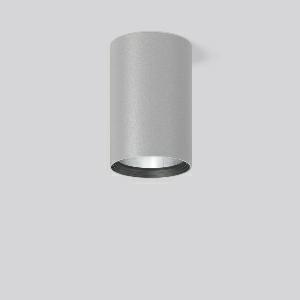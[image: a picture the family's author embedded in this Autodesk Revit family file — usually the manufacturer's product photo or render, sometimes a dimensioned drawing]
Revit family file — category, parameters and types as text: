
# Revit family: heledon_maxi_a_931225_004_2_fa69
name_source: partatom
category: Lighting Fixtures
units: mm (PartAtom-declared; Revit-internal decimal feet)

## family parameters
Cut with Voids When Loaded = No
Host = Face
Light Source = No
Part Type = Normal
Room Calculation Point = No
Round Connector Dimension = Use Diameter
Shared = No

## types (1)
- HELEDON maxi A (1 x LED Modul 927, 4100 lm, 2700)
    Apparent Load = 35 VA
    Approval mark = CE
    CIE Flux Codes = 100 100 100 100 100
    Color Rendering = 92
    Color Temperature = 2700
    Default Elevation = 1800 mm
    Description = Series: HELEDON maxi
Cylindrical surface-mounted downlight. Housing: die-cast aluminium, powder-coated. Internal ceiling frame polycarbonate with bayonet mounting. Black plastic ring and recessed LED to prevent glare from the side. Optical assembly with reflector made of MIRO-Silver with 98% total light reflection for outstanding efficiency - can be changed without tools. Best colour rendering index Ra>90. Suitable for Ceiling mounting. Easy installation with a separate ceiling frame with bayonet mounting and plug connection. Driver integrated. Connected via plug-in connector. High quality converter without flickering and stroboscopic effect. The following accessories can be mounted without use of tools: interchangeable lenses, decorative glasses, honeycomb louvre, clear and frosted diffusers, white interchangeable plastic ring. 
Colour: silver
Diameter: 123 mm
Height: 183 mm
Lamp: LED
Socket: without socket
Colour temperature: 2700K
Colour rendering index (CRI): 92
System power: 35 W
Rated luminous flux: 4100 lm
Luminous efficiency: 117 lm/W
Control gear: Regulated power supply
Protection class: I
Type of protection: IP 20
    Height = 183 mm
    Lamp = 1 x LED Modul 927
    Lamp Light Flux = 4100 lm
    Lamp count = 1
    Length = 123 mm
    Lifetime = 50000 h
    Luminous efficacy = 117 lm/W
    Manufacturer = RZB
    ModVariant = No
    Model = 931225.004.2
    Mounting Place = Ceiling
    Mounting Type = Surface mounted
    Number of Poles = 1
    OnlyDefault = Yes
    Power Factor = 1
    Product Name = HELEDON maxi A
    Product group = Surface mounted downlights
    ProductGroupID = 302
    Protection Class = Protection class I
    Protection Degree = IP 20
    RLX_Detail_Level = 1
    RLX_Emergency_Light_Flux = 0 lm
    RLX_Emergency_Type = 0
    RLX_Emergency_Type_DB = No
    RlxData = <blob elided: 99285 chars, md5=a1d069c4>
    Socket = socket
    Standby Power = 0 W
    System Light Flux = 4100 lm
    System Power = 35 W
    Type Comments = Product without accessories
    Type Image = 931192.004.jpg
    URL = http://relux.com
    VarID = ---
    Voltage = 230 V
    Voltage Range = 220-240 V
    Weight = 0.00 kg
    Width = 0 mm  [stored 0 ft]

note: [stored X ft] marks values corroborated as IEEE doubles in the binary element streams (Revit-internal decimal feet)

## geometry (parser evidence)
native form markers: Blend x4, Sweep x11
no freeform markers — native parametric forms only
